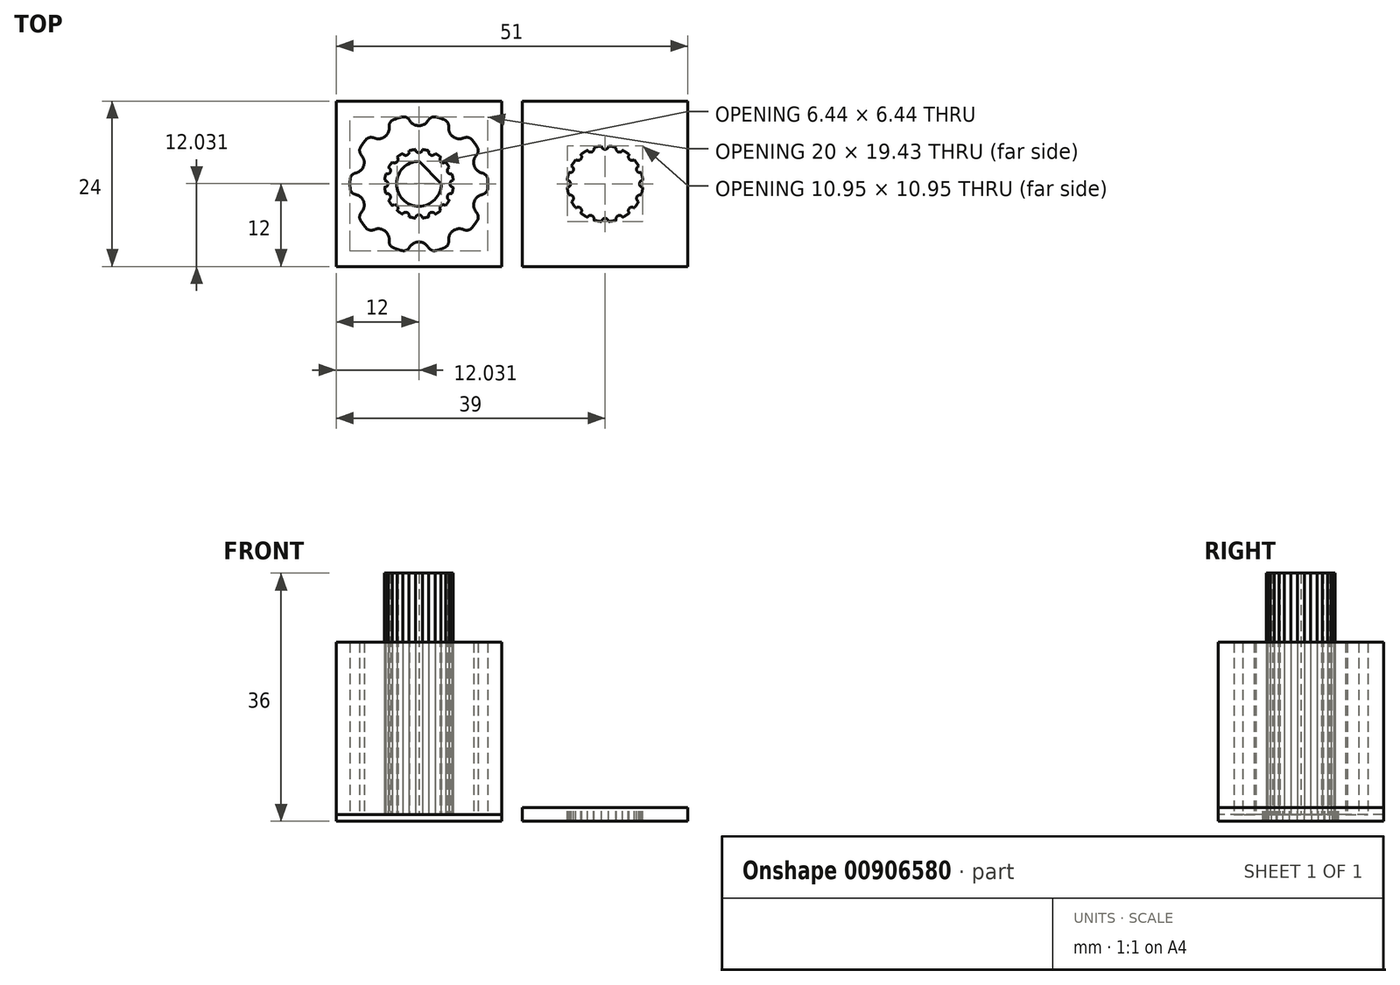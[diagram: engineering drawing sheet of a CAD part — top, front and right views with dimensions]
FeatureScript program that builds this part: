
annotation { "Feature Type Name" : "Feature", "Feature Type Description" : "" }
export const myFeature = defineFeature(function(context is Context, id is Id, definition is map)
    precondition{}
    {
        {
            var Q0;
            Q0=qCreatedBy(makeId("Top.planeOp"),FACE);
            var sketch = newSketch(context, id + "F0", { "sketchPlane" : qUnion([Q0])});
            skArc(sketch, "E0", {"start": v(-2.48, 9.69) * mm, "mid": v(-3.1, 9.51) * mm, "end": v(-3.7, 9.3) * mm});
            skLineSegment(sketch, "E1", {"start": v(0, 0) * mm, "end": v(0, 10) * mm, "construction": true});
            skArc(sketch, "E2", {"start": v(-1.36, 9.22) * mm, "mid": v(0, 8.43) * mm, "end": v(1.36, 9.22) * mm});
            skArc(sketch, "E3.1.0", {"start": v(-6.52, 6.66) * mm, "mid": v(-4.95, 6.82) * mm, "end": v(-4.32, 8.26) * mm});
            skArc(sketch, "E3.2.0", {"start": v(-9.19, 1.55) * mm, "mid": v(-8.02, 2.6) * mm, "end": v(-8.35, 4.14) * mm});
            skArc(sketch, "E3.3.0", {"start": v(-8.35, -4.14) * mm, "mid": v(-8.02, -2.6) * mm, "end": v(-9.19, -1.55) * mm});
            skArc(sketch, "E3.4.0", {"start": v(-4.32, -8.26) * mm, "mid": v(-4.95, -6.82) * mm, "end": v(-6.52, -6.66) * mm});
            skArc(sketch, "E3.5.0", {"start": v(1.36, -9.22) * mm, "mid": v(0, -8.43) * mm, "end": v(-1.36, -9.22) * mm});
            skArc(sketch, "E3.6.0", {"start": v(6.52, -6.66) * mm, "mid": v(4.95, -6.82) * mm, "end": v(4.32, -8.26) * mm});
            skArc(sketch, "E3.7.0", {"start": v(9.19, -1.55) * mm, "mid": v(8.02, -2.6) * mm, "end": v(8.35, -4.14) * mm});
            skArc(sketch, "E3.8.0", {"start": v(8.35, 4.14) * mm, "mid": v(8.02, 2.6) * mm, "end": v(9.19, 1.55) * mm});
            skArc(sketch, "E3.9.0", {"start": v(4.32, 8.26) * mm, "mid": v(4.95, 6.82) * mm, "end": v(6.52, 6.66) * mm});
            skArc(sketch, "E4.trimOffspring", {"start": v(3.7, 9.3) * mm, "mid": v(3.1, 9.51) * mm, "end": v(2.48, 9.69) * mm});
            skArc(sketch, "E5.trimOffspring", {"start": v(8.45, 5.35) * mm, "mid": v(8.1, 5.88) * mm, "end": v(7.7, 6.38) * mm});
            skArc(sketch, "E6.trimOffspring", {"start": v(9.98, -0.64) * mm, "mid": v(10, 0) * mm, "end": v(9.98, 0.64) * mm});
            skArc(sketch, "E7.trimOffspring", {"start": v(7.7, -6.38) * mm, "mid": v(8.1, -5.88) * mm, "end": v(8.45, -5.35) * mm});
            skArc(sketch, "E8.trimOffspring", {"start": v(2.48, -9.69) * mm, "mid": v(3.1, -9.51) * mm, "end": v(3.7, -9.3) * mm});
            skArc(sketch, "E9.trimOffspring", {"start": v(-3.7, -9.3) * mm, "mid": v(-3.1, -9.51) * mm, "end": v(-2.48, -9.69) * mm});
            skArc(sketch, "E10.trimOffspring", {"start": v(-8.45, -5.35) * mm, "mid": v(-8.1, -5.88) * mm, "end": v(-7.7, -6.38) * mm});
            skArc(sketch, "E11.trimOffspring", {"start": v(-9.98, 0.64) * mm, "mid": v(-10, 0) * mm, "end": v(-9.98, -0.64) * mm});
            skPoint(sketch, "E12.visualSharp", {"position": v(1.57, 9.88) * mm});
            skArc(sketch, "E12.filletArc", {"start": v(2.48, 9.69) * mm, "mid": v(1.84, 9.64) * mm, "end": v(1.36, 9.22) * mm});
            skPoint(sketch, "E13.visualSharp", {"position": v(4.54, 8.91) * mm});
            skArc(sketch, "E13.filletArc", {"start": v(4.32, 8.26) * mm, "mid": v(4.18, 8.88) * mm, "end": v(3.7, 9.3) * mm});
            skPoint(sketch, "E14.visualSharp", {"position": v(7.07, 7.07) * mm});
            skArc(sketch, "E14.filletArc", {"start": v(7.7, 6.38) * mm, "mid": v(7.16, 6.72) * mm, "end": v(6.52, 6.66) * mm});
            skPoint(sketch, "E15.visualSharp", {"position": v(8.9, 4.54) * mm});
            skArc(sketch, "E15.filletArc", {"start": v(8.35, 4.14) * mm, "mid": v(8.6, 4.73) * mm, "end": v(8.45, 5.35) * mm});
            skPoint(sketch, "E16.visualSharp", {"position": v(9.88, 1.56) * mm});
            skArc(sketch, "E16.filletArc", {"start": v(9.98, 0.64) * mm, "mid": v(9.74, 1.23) * mm, "end": v(9.19, 1.55) * mm});
            skPoint(sketch, "E17.visualSharp", {"position": v(9.88, -1.56) * mm});
            skArc(sketch, "E17.filletArc", {"start": v(9.19, -1.55) * mm, "mid": v(9.74, -1.23) * mm, "end": v(9.98, -0.64) * mm});
            skPoint(sketch, "E18.visualSharp", {"position": v(8.9, -4.54) * mm});
            skArc(sketch, "E18.filletArc", {"start": v(8.45, -5.35) * mm, "mid": v(8.6, -4.73) * mm, "end": v(8.35, -4.14) * mm});
            skPoint(sketch, "E19.visualSharp", {"position": v(7.07, -7.07) * mm});
            skArc(sketch, "E19.filletArc", {"start": v(6.52, -6.66) * mm, "mid": v(7.16, -6.72) * mm, "end": v(7.7, -6.38) * mm});
            skPoint(sketch, "E20.visualSharp", {"position": v(4.54, -8.91) * mm});
            skArc(sketch, "E20.filletArc", {"start": v(3.7, -9.3) * mm, "mid": v(4.18, -8.88) * mm, "end": v(4.32, -8.26) * mm});
            skPoint(sketch, "E21.visualSharp", {"position": v(1.57, -9.88) * mm});
            skArc(sketch, "E21.filletArc", {"start": v(1.36, -9.22) * mm, "mid": v(1.84, -9.64) * mm, "end": v(2.48, -9.69) * mm});
            skPoint(sketch, "E22.visualSharp", {"position": v(-1.57, -9.88) * mm});
            skArc(sketch, "E22.filletArc", {"start": v(-2.48, -9.69) * mm, "mid": v(-1.84, -9.64) * mm, "end": v(-1.36, -9.22) * mm});
            skPoint(sketch, "E23.visualSharp", {"position": v(-4.54, -8.91) * mm});
            skArc(sketch, "E23.filletArc", {"start": v(-4.32, -8.26) * mm, "mid": v(-4.18, -8.88) * mm, "end": v(-3.7, -9.3) * mm});
            skPoint(sketch, "E24.visualSharp", {"position": v(-7.07, -7.07) * mm});
            skArc(sketch, "E24.filletArc", {"start": v(-7.7, -6.38) * mm, "mid": v(-7.16, -6.72) * mm, "end": v(-6.52, -6.66) * mm});
            skPoint(sketch, "E25.visualSharp", {"position": v(-8.9, -4.54) * mm});
            skArc(sketch, "E25.filletArc", {"start": v(-8.35, -4.14) * mm, "mid": v(-8.6, -4.73) * mm, "end": v(-8.45, -5.35) * mm});
            skPoint(sketch, "E26.visualSharp", {"position": v(-9.88, -1.56) * mm});
            skArc(sketch, "E26.filletArc", {"start": v(-9.98, -0.64) * mm, "mid": v(-9.74, -1.23) * mm, "end": v(-9.19, -1.55) * mm});
            skPoint(sketch, "E27.visualSharp", {"position": v(-9.88, 1.56) * mm});
            skArc(sketch, "E27.filletArc", {"start": v(-9.19, 1.55) * mm, "mid": v(-9.74, 1.23) * mm, "end": v(-9.98, 0.64) * mm});
            skPoint(sketch, "E28.visualSharp", {"position": v(-8.9, 4.54) * mm});
            skArc(sketch, "E28.filletArc", {"start": v(-8.45, 5.35) * mm, "mid": v(-8.6, 4.73) * mm, "end": v(-8.35, 4.14) * mm});
            skArc(sketch, "E29.trimOffspring", {"start": v(-7.7, 6.38) * mm, "mid": v(-8.1, 5.88) * mm, "end": v(-8.45, 5.35) * mm});
            skPoint(sketch, "E30.visualSharp", {"position": v(-7.07, 7.07) * mm});
            skArc(sketch, "E30.filletArc", {"start": v(-6.52, 6.66) * mm, "mid": v(-7.16, 6.72) * mm, "end": v(-7.7, 6.38) * mm});
            skPoint(sketch, "E31.visualSharp", {"position": v(-4.54, 8.91) * mm});
            skArc(sketch, "E31.filletArc", {"start": v(-3.7, 9.3) * mm, "mid": v(-4.18, 8.88) * mm, "end": v(-4.32, 8.26) * mm});
            skPoint(sketch, "E32.visualSharp", {"position": v(-1.57, 9.88) * mm});
            skArc(sketch, "E32.filletArc", {"start": v(-1.36, 9.22) * mm, "mid": v(-1.84, 9.64) * mm, "end": v(-2.48, 9.69) * mm});
            skArc(sketch, "E33", {"start": v(0, 3.25) * mm, "mid": v(-2.3, -2.3) * mm, "end": v(3.25, 0) * mm});
            skLineSegment(sketch, "E34", {"start": v(0, 3.25) * mm, "end": v(3.25, 0) * mm});
            skLineSegment(sketch, "E35", {"start": v(12, 0) * mm, "end": v(12, 12) * mm});
            skLineSegment(sketch, "E36", {"start": v(12, 12) * mm, "end": v(-12, 12) * mm});
            skLineSegment(sketch, "E37", {"start": v(-12, 12) * mm, "end": v(-12, -12) * mm});
            skLineSegment(sketch, "E38", {"start": v(-12, -12) * mm, "end": v(12, -12) * mm});
            skLineSegment(sketch, "E39", {"start": v(12, -12) * mm, "end": v(12, 0) * mm});
            skArc(sketch, "E40", {"start": v(-0.5, 4.97) * mm, "mid": v(-0.98, 4.9) * mm, "end": v(-1.44, 4.79) * mm});
            skArc(sketch, "E41", {"start": v(-0.5, 4.98) * mm, "mid": v(0, 4.5) * mm, "end": v(0.5, 4.98) * mm});
            skArc(sketch, "E42.1.0", {"start": v(-2.37, 4.4) * mm, "mid": v(-1.72, 4.16) * mm, "end": v(-1.44, 4.79) * mm});
            skArc(sketch, "E42.2.0", {"start": v(-3.87, 3.16) * mm, "mid": v(-3.18, 3.18) * mm, "end": v(-3.16, 3.87) * mm});
            skArc(sketch, "E42.3.0", {"start": v(-4.79, 1.44) * mm, "mid": v(-4.16, 1.72) * mm, "end": v(-4.4, 2.37) * mm});
            skArc(sketch, "E42.4.0", {"start": v(-4.98, -0.5) * mm, "mid": v(-4.5, 0) * mm, "end": v(-4.98, 0.5) * mm});
            skArc(sketch, "E42.5.0", {"start": v(-4.4, -2.37) * mm, "mid": v(-4.16, -1.72) * mm, "end": v(-4.79, -1.44) * mm});
            skArc(sketch, "E42.6.0", {"start": v(-3.16, -3.87) * mm, "mid": v(-3.18, -3.18) * mm, "end": v(-3.87, -3.16) * mm});
            skArc(sketch, "E42.7.0", {"start": v(-1.44, -4.79) * mm, "mid": v(-1.72, -4.16) * mm, "end": v(-2.37, -4.4) * mm});
            skArc(sketch, "E42.8.0", {"start": v(0.5, -4.98) * mm, "mid": v(0, -4.5) * mm, "end": v(-0.5, -4.98) * mm});
            skArc(sketch, "E42.9.0", {"start": v(2.37, -4.4) * mm, "mid": v(1.72, -4.16) * mm, "end": v(1.44, -4.79) * mm});
            skArc(sketch, "E42.10.0", {"start": v(3.87, -3.16) * mm, "mid": v(3.18, -3.18) * mm, "end": v(3.16, -3.87) * mm});
            skArc(sketch, "E42.11.0", {"start": v(4.79, -1.44) * mm, "mid": v(4.16, -1.72) * mm, "end": v(4.4, -2.37) * mm});
            skArc(sketch, "E42.12.0", {"start": v(4.98, 0.5) * mm, "mid": v(4.5, 0) * mm, "end": v(4.98, -0.5) * mm});
            skArc(sketch, "E42.13.0", {"start": v(4.4, 2.37) * mm, "mid": v(4.16, 1.72) * mm, "end": v(4.79, 1.44) * mm});
            skArc(sketch, "E42.14.0", {"start": v(3.16, 3.87) * mm, "mid": v(3.18, 3.18) * mm, "end": v(3.87, 3.16) * mm});
            skArc(sketch, "E42.15.0", {"start": v(1.44, 4.79) * mm, "mid": v(1.72, 4.16) * mm, "end": v(2.37, 4.4) * mm});
            skArc(sketch, "E43.trimOffspring", {"start": v(1.44, 4.79) * mm, "mid": v(0.98, 4.9) * mm, "end": v(0.5, 4.98) * mm});
            skArc(sketch, "E44.trimOffspring", {"start": v(3.16, 3.87) * mm, "mid": v(2.78, 4.16) * mm, "end": v(2.37, 4.4) * mm});
            skArc(sketch, "E45.trimOffspring", {"start": v(4.4, 2.37) * mm, "mid": v(4.16, 2.78) * mm, "end": v(3.87, 3.16) * mm});
            skArc(sketch, "E46.trimOffspring", {"start": v(4.98, 0.5) * mm, "mid": v(4.9, 0.98) * mm, "end": v(4.79, 1.44) * mm});
            skArc(sketch, "E47.trimOffspring", {"start": v(4.79, -1.44) * mm, "mid": v(4.9, -0.98) * mm, "end": v(4.97, -0.5) * mm});
            skArc(sketch, "E48.trimOffspring", {"start": v(3.87, -3.16) * mm, "mid": v(4.16, -2.78) * mm, "end": v(4.4, -2.37) * mm});
            skArc(sketch, "E49.trimOffspring", {"start": v(2.37, -4.4) * mm, "mid": v(2.78, -4.16) * mm, "end": v(3.16, -3.87) * mm});
            skArc(sketch, "E50.trimOffspring", {"start": v(0.5, -4.98) * mm, "mid": v(0.98, -4.9) * mm, "end": v(1.44, -4.79) * mm});
            skArc(sketch, "E51.trimOffspring", {"start": v(-1.44, -4.79) * mm, "mid": v(-0.98, -4.9) * mm, "end": v(-0.5, -4.98) * mm});
            skArc(sketch, "E52.trimOffspring", {"start": v(-3.16, -3.87) * mm, "mid": v(-2.78, -4.16) * mm, "end": v(-2.37, -4.4) * mm});
            skArc(sketch, "E53.trimOffspring", {"start": v(-4.4, -2.37) * mm, "mid": v(-4.16, -2.78) * mm, "end": v(-3.87, -3.16) * mm});
            skArc(sketch, "E54.trimOffspring", {"start": v(-4.98, -0.5) * mm, "mid": v(-4.9, -0.98) * mm, "end": v(-4.79, -1.44) * mm});
            skArc(sketch, "E55.trimOffspring", {"start": v(-4.79, 1.44) * mm, "mid": v(-4.9, 0.98) * mm, "end": v(-4.98, 0.5) * mm});
            skArc(sketch, "E56.trimOffspring", {"start": v(-3.87, 3.16) * mm, "mid": v(-4.16, 2.78) * mm, "end": v(-4.4, 2.37) * mm});
            skArc(sketch, "E57.trimOffspring", {"start": v(-2.37, 4.4) * mm, "mid": v(-2.78, 4.16) * mm, "end": v(-3.16, 3.87) * mm});
            skSolve(sketch);
        }
        {
            var Q0;
            Q0=qCreatedBy(makeId("Top.planeOp"),FACE);
            var sketch = newSketch(context, id + "F1", { "sketchPlane" : qUnion([Q0])});
            skLineSegment(sketch, "E58", {"start": v(12, 0) * mm, "end": v(12, -12) * mm});
            skLineSegment(sketch, "E59", {"start": v(12, -12) * mm, "end": v(-12, -12) * mm});
            skLineSegment(sketch, "E60", {"start": v(-12, -12) * mm, "end": v(-12, 12) * mm});
            skLineSegment(sketch, "E61", {"start": v(-12, 12) * mm, "end": v(12, 12) * mm});
            skLineSegment(sketch, "E62", {"start": v(12, 12) * mm, "end": v(12, 0) * mm});
            skSolve(sketch);
        }
        {
            var Q0;
            Q0=qCreatedBy(makeId("Top.planeOp"),FACE);
            var sketch = newSketch(context, id + "F2", { "sketchPlane" : qUnion([Q0])});
            skLineSegment(sketch, "E63", {"start": v(0, 0) * mm, "end": v(15, 0) * mm, "construction": true});
            skLineSegment(sketch, "E64", {"start": v(15, 0) * mm, "end": v(15, 12) * mm});
            skLineSegment(sketch, "E65", {"start": v(15, 12) * mm, "end": v(39, 12) * mm});
            skLineSegment(sketch, "E66", {"start": v(39, 12) * mm, "end": v(39, -12) * mm});
            skLineSegment(sketch, "E67", {"start": v(39, -12) * mm, "end": v(15, -12) * mm});
            skLineSegment(sketch, "E68", {"start": v(15, -12) * mm, "end": v(15, 0) * mm});
            skLineSegment(sketch, "E69", {"start": v(15, -12) * mm, "end": v(27, 0) * mm, "construction": true});
            skLineSegment(sketch, "E70", {"start": v(39, -12) * mm, "end": v(15, 12) * mm, "construction": true});
            skLineSegment(sketch, "E71", {"start": v(26.97, 0.03) * mm, "end": v(26.97, 10.03) * mm, "construction": true});
            skPoint(sketch, "E72.center", {"position": v(27.5, 0) * mm});
            skArc(sketch, "E73", {"start": v(26.5, 5.48) * mm, "mid": v(25.93, 5.4) * mm, "end": v(25.37, 5.25) * mm});
            skArc(sketch, "E74", {"start": v(26.5, 5.48) * mm, "mid": v(27, 5) * mm, "end": v(27.5, 5.48) * mm});
            skArc(sketch, "E75.1.0", {"start": v(24.44, 4.87) * mm, "mid": v(25.09, 4.62) * mm, "end": v(25.37, 5.25) * mm});
            skArc(sketch, "E75.2.0", {"start": v(22.77, 3.52) * mm, "mid": v(23.46, 3.54) * mm, "end": v(23.48, 4.23) * mm});
            skArc(sketch, "E75.3.0", {"start": v(21.75, 1.63) * mm, "mid": v(22.38, 1.91) * mm, "end": v(22.13, 2.56) * mm});
            skArc(sketch, "E75.4.0", {"start": v(21.52, -0.5) * mm, "mid": v(22, 0) * mm, "end": v(21.52, 0.5) * mm});
            skArc(sketch, "E75.5.0", {"start": v(22.13, -2.56) * mm, "mid": v(22.38, -1.91) * mm, "end": v(21.75, -1.63) * mm});
            skArc(sketch, "E75.6.0", {"start": v(23.48, -4.23) * mm, "mid": v(23.46, -3.54) * mm, "end": v(22.77, -3.52) * mm});
            skArc(sketch, "E75.7.0", {"start": v(25.37, -5.25) * mm, "mid": v(25.09, -4.62) * mm, "end": v(24.44, -4.87) * mm});
            skArc(sketch, "E75.8.0", {"start": v(27.5, -5.48) * mm, "mid": v(27, -5) * mm, "end": v(26.5, -5.48) * mm});
            skArc(sketch, "E75.9.0", {"start": v(29.56, -4.87) * mm, "mid": v(28.91, -4.62) * mm, "end": v(28.63, -5.25) * mm});
            skArc(sketch, "E75.10.0", {"start": v(31.23, -3.52) * mm, "mid": v(30.54, -3.54) * mm, "end": v(30.52, -4.23) * mm});
            skArc(sketch, "E75.11.0", {"start": v(32.25, -1.63) * mm, "mid": v(31.62, -1.91) * mm, "end": v(31.87, -2.56) * mm});
            skArc(sketch, "E75.12.0", {"start": v(32.48, 0.5) * mm, "mid": v(32, 0) * mm, "end": v(32.48, -0.5) * mm});
            skArc(sketch, "E75.13.0", {"start": v(31.87, 2.56) * mm, "mid": v(31.62, 1.91) * mm, "end": v(32.25, 1.63) * mm});
            skArc(sketch, "E75.14.0", {"start": v(30.52, 4.23) * mm, "mid": v(30.54, 3.54) * mm, "end": v(31.23, 3.52) * mm});
            skArc(sketch, "E75.15.0", {"start": v(28.63, 5.25) * mm, "mid": v(28.91, 4.62) * mm, "end": v(29.56, 4.87) * mm});
            skArc(sketch, "E76.trimOffspring", {"start": v(28.63, 5.25) * mm, "mid": v(28.07, 5.4) * mm, "end": v(27.5, 5.48) * mm});
            skArc(sketch, "E77.trimOffspring", {"start": v(30.52, 4.23) * mm, "mid": v(30.06, 4.57) * mm, "end": v(29.56, 4.87) * mm});
            skArc(sketch, "E78.trimOffspring", {"start": v(31.87, 2.56) * mm, "mid": v(31.57, 3.06) * mm, "end": v(31.23, 3.52) * mm});
            skArc(sketch, "E79.trimOffspring", {"start": v(32.48, 0.5) * mm, "mid": v(32.4, 1.07) * mm, "end": v(32.25, 1.63) * mm});
            skArc(sketch, "E80.trimOffspring", {"start": v(32.25, -1.63) * mm, "mid": v(32.4, -1.07) * mm, "end": v(32.48, -0.5) * mm});
            skArc(sketch, "E81.trimOffspring", {"start": v(31.23, -3.52) * mm, "mid": v(31.57, -3.06) * mm, "end": v(31.87, -2.56) * mm});
            skArc(sketch, "E82.trimOffspring", {"start": v(29.56, -4.87) * mm, "mid": v(30.06, -4.57) * mm, "end": v(30.52, -4.23) * mm});
            skArc(sketch, "E83.trimOffspring", {"start": v(27.5, -5.48) * mm, "mid": v(28.07, -5.4) * mm, "end": v(28.63, -5.25) * mm});
            skArc(sketch, "E84.trimOffspring", {"start": v(25.37, -5.25) * mm, "mid": v(25.93, -5.4) * mm, "end": v(26.5, -5.48) * mm});
            skArc(sketch, "E85.trimOffspring", {"start": v(23.48, -4.23) * mm, "mid": v(23.94, -4.57) * mm, "end": v(24.44, -4.87) * mm});
            skArc(sketch, "E86.trimOffspring", {"start": v(22.13, -2.56) * mm, "mid": v(22.43, -3.06) * mm, "end": v(22.77, -3.52) * mm});
            skArc(sketch, "E87.trimOffspring", {"start": v(21.52, -0.5) * mm, "mid": v(21.6, -1.07) * mm, "end": v(21.75, -1.63) * mm});
            skArc(sketch, "E88.trimOffspring", {"start": v(21.75, 1.63) * mm, "mid": v(21.6, 1.07) * mm, "end": v(21.52, 0.5) * mm});
            skArc(sketch, "E89.trimOffspring", {"start": v(22.77, 3.52) * mm, "mid": v(22.43, 3.06) * mm, "end": v(22.13, 2.56) * mm});
            skArc(sketch, "E90.trimOffspring", {"start": v(24.44, 4.87) * mm, "mid": v(23.94, 4.57) * mm, "end": v(23.48, 4.23) * mm});
            skLineSegment(sketch, "E91.trimOffspring", {"start": v(28.62, 1.63) * mm, "end": v(39, 12) * mm, "construction": true});
            skSolve(sketch);
        }
        {
            var Q0;
            Q0 = qSketchRegion(id + "F0", true);
            extrude(context, id + "F3", {"entities" : qUnion([Q0]), "depth" : 25 * mm, "offsetDistance" : 25 * mm});
        }
        {
            var Q0;
            Q0=makeQuery(id+"F0.imprint","IMPRINT",FACE,{"disambiguationData":[TD([[makeQuery(id+"F0.imprint","IMPRINT",EDGE,{"derivedFrom":sQuery(id+"F0.wireOp",EDGE,"E33")}),-1.0]])]});
            extrude(context, id + "F4", {"entities" : qUnion([Q0]), "depth" : 35 * mm, "offsetDistance" : 25 * mm});
        }
        {
            var Q0;
            Q0=makeQuery(id+"F1.imprint","IMPRINT",FACE,{"disambiguationData":[TD([[makeQuery(id+"F1.imprint","IMPRINT",EDGE,{"derivedFrom":sQuery(id+"F1.wireOp",EDGE,"E58")}),-1.0]])]});
            extrude(context, id + "F5", {"entities" : qUnion([Q0]), "oppositeDirection" : true, "depth" : 1 * mm, "offsetDistance" : 25 * mm});
        }
        {
            var Q0;
            Q0=makeQuery(id+"F2.imprint","IMPRINT",FACE,{"disambiguationData":[TD([[makeQuery(id+"F2.imprint","IMPRINT",EDGE,{"derivedFrom":sQuery(id+"F2.wireOp",EDGE,"E64")}),-1.0]])]});
            extrude(context, id + "F6", {"entities" : qUnion([Q0]), "oppositeDirection" : true, "depth" : 1 * mm, "offsetDistance" : 25 * mm, "hasSecondDirection" : true, "secondDirectionOppositeDirection" : false, "secondDirectionDepth" : 1 * mm});
        }
    });
